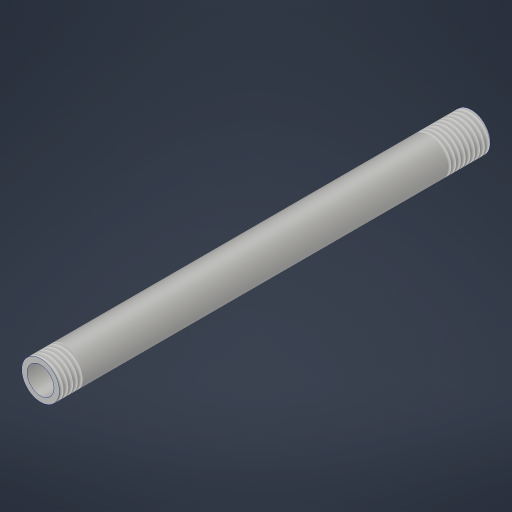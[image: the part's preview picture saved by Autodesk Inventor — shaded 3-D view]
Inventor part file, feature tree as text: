
AUTODESK INVENTOR PART (.ipt)
format: ipt  version: 2023.4 (Build 274418000, 418)  size: 200,192 bytes
history: native  units: in
note: dims shown in document units (in); Inventor stores cm internally (conversion verified against a paired STEP export)
features: thread x2, extrude x1, sketch x1
ambient origin geometry x8: Origin, YZ Plane, XZ Plane, XY Plane, X Axis, Y Axis, Z Axis, Center Point
bodies: Solid1 (feature_tree)
feature tree (4):
  extrude  "Extrusion1"  Depth=10.0in
  thread  "Thread1"  [1 undecoded]
  thread  "Thread2"  [1 undecoded]
  sketch  "Sketch1"  dims[d0=0.875in d1=0.125in d2=10.0in d3=0.0in d4=1.0in d5=0.0in d6=0.567in d7=0.0in]
note: 2 required parameter values undecoded (feature->parameter linkage not recoverable at this tier; creation-order binding heuristic only, values carry confidence <= 0.55)
